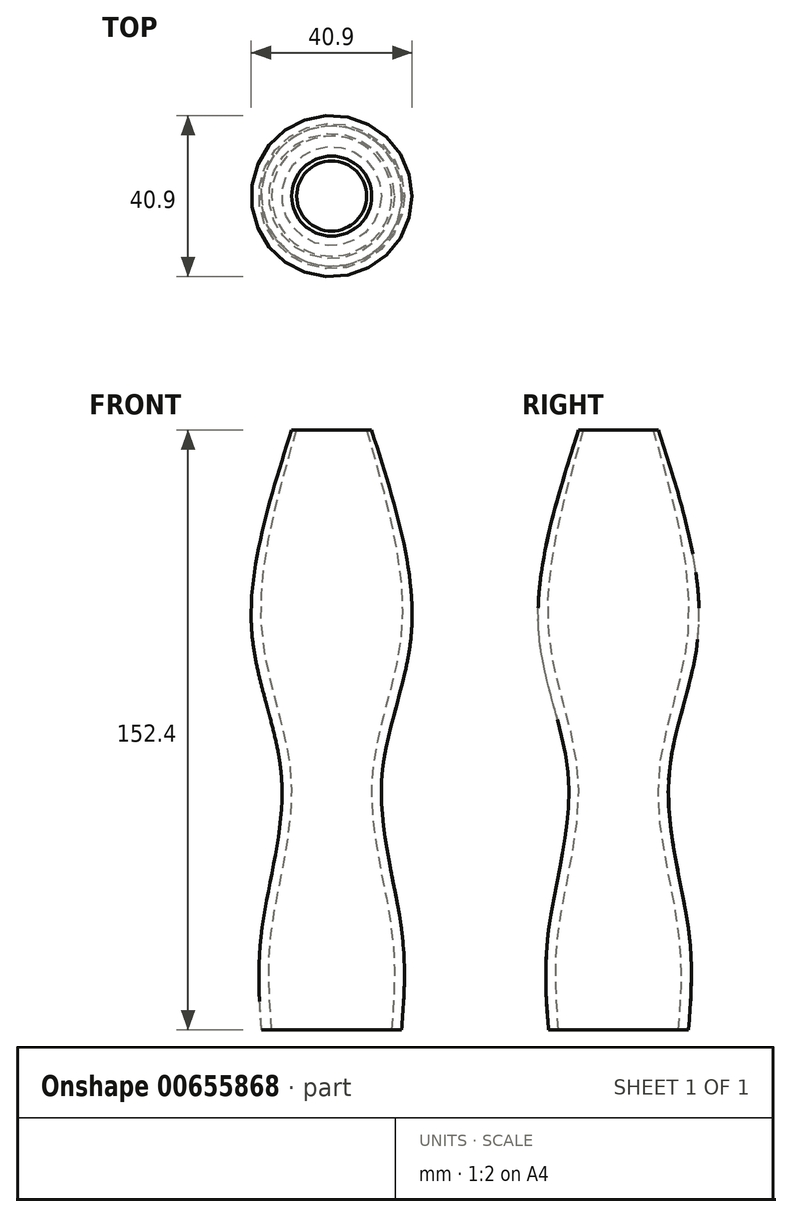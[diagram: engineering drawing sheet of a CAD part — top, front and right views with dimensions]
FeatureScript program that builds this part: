
annotation { "Feature Type Name" : "Feature", "Feature Type Description" : "" }
export const myFeature = defineFeature(function(context is Context, id is Id, definition is map)
    precondition{}
    {
        {
            var Q0;
            Q0=qCreatedBy(makeId("Front.planeOp"),FACE);
            var sketch = newSketch(context, id + "F0", { "sketchPlane" : qUnion([Q0])});
            skLineSegment(sketch, "E0", {"start": v(12.7, -17.4) * mm, "end": v(12.7, -17.4) * mm});
            skLineSegment(sketch, "E1", {"start": v(17.65, -80.9) * mm, "end": v(17.78, -80.9) * mm});
            skFitSpline(sketch, "E2", {"points": [v(-10.16, 71.5) * mm, v(-20.32, 20.7) * mm, v(-12.7, -17.4) * mm, v(-17.78, -55.5) * mm, v(-17.78, -80.9) * mm], "startDerivative": vector(-57.7, -181.43) * mm, "endDerivative": vector(9.08, -117.34) * mm});
            skFitSpline(sketch, "E3", {"points": [v(-8.9, 71.5) * mm, v(-17.78, 20.7) * mm, v(-10.16, -17.4) * mm, v(-15.24, -55.5) * mm, v(-15.24, -80.9) * mm], "startDerivative": vector(-52.14, -181.81) * mm, "endDerivative": vector(9.01, -117.26) * mm});
            skLineSegment(sketch, "E4", {"start": v(-10.16, 71.5) * mm, "end": v(-8.9, 71.5) * mm});
            skFitSpline(sketch, "E5", {"points": [v(10.16, 71.5) * mm, v(20.32, 20.7) * mm, v(12.7, -17.4) * mm, v(17.78, -55.5) * mm, v(17.78, -80.9) * mm], "startDerivative": vector(57.7, -181.43) * mm, "endDerivative": vector(-9.08, -117.34) * mm});
            skPoint(sketch, "E6.end.orphan", {"position": v(0, 71.5) * mm});
            skFitSpline(sketch, "E7", {"points": [v(8.89, 71.5) * mm, v(17.78, 20.7) * mm, v(10.16, -17.4) * mm, v(15.24, -55.5) * mm, v(15.24, -80.9) * mm], "startDerivative": vector(52.14, -181.81) * mm, "endDerivative": vector(-9.01, -117.26) * mm});
            skLineSegment(sketch, "E8", {"start": v(8.89, 71.5) * mm, "end": v(10.16, 71.5) * mm});
            skPoint(sketch, "E9.start.orphan", {"position": v(0, -55.5) * mm});
            skPoint(sketch, "E10.start.orphan", {"position": v(0, -80.9) * mm});
            skLineSegment(sketch, "E11", {"start": v(0, 71.5) * mm, "end": v(0, -80.9) * mm, "construction": true});
            skLineSegment(sketch, "E12", {"start": v(-17.78, -80.9) * mm, "end": v(-15.24, -80.9) * mm});
            skLineSegment(sketch, "E13", {"start": v(15.24, -80.9) * mm, "end": v(17.78, -80.9) * mm});
            skSolve(sketch);
        }
        {
            var Q0;
            Q0=makeQuery(id+"F0.imprint","IMPRINT",FACE,{"disambiguationData":[TD([[makeQuery(id+"F0.imprint","IMPRINT",EDGE,{"derivedFrom":sQuery(id+"F0.wireOp",EDGE,"E2")}),1.0]])]});
            var Q1;
            {var subQ1=sQuery(id+"F0.wireOp",EDGE,"E7");Q1=makeQuery(id+"F0.imprint","IMPRINT",FACE,{"disambiguationData":[TD([[makeQuery(id+"F0.imprint","IMPRINT",EDGE,{"derivedFrom":subQ1}),1.0]])]});}
            var Q2;
            Q2=sQuery(id+"F0.wireOp",EDGE,"E11");
            revolve(context, id + "F1", {"entities" : qUnion([Q0, Q1]), "axis" : qUnion([Q2]), "revolveType" : RevolveType.FULL});
        }
    });
